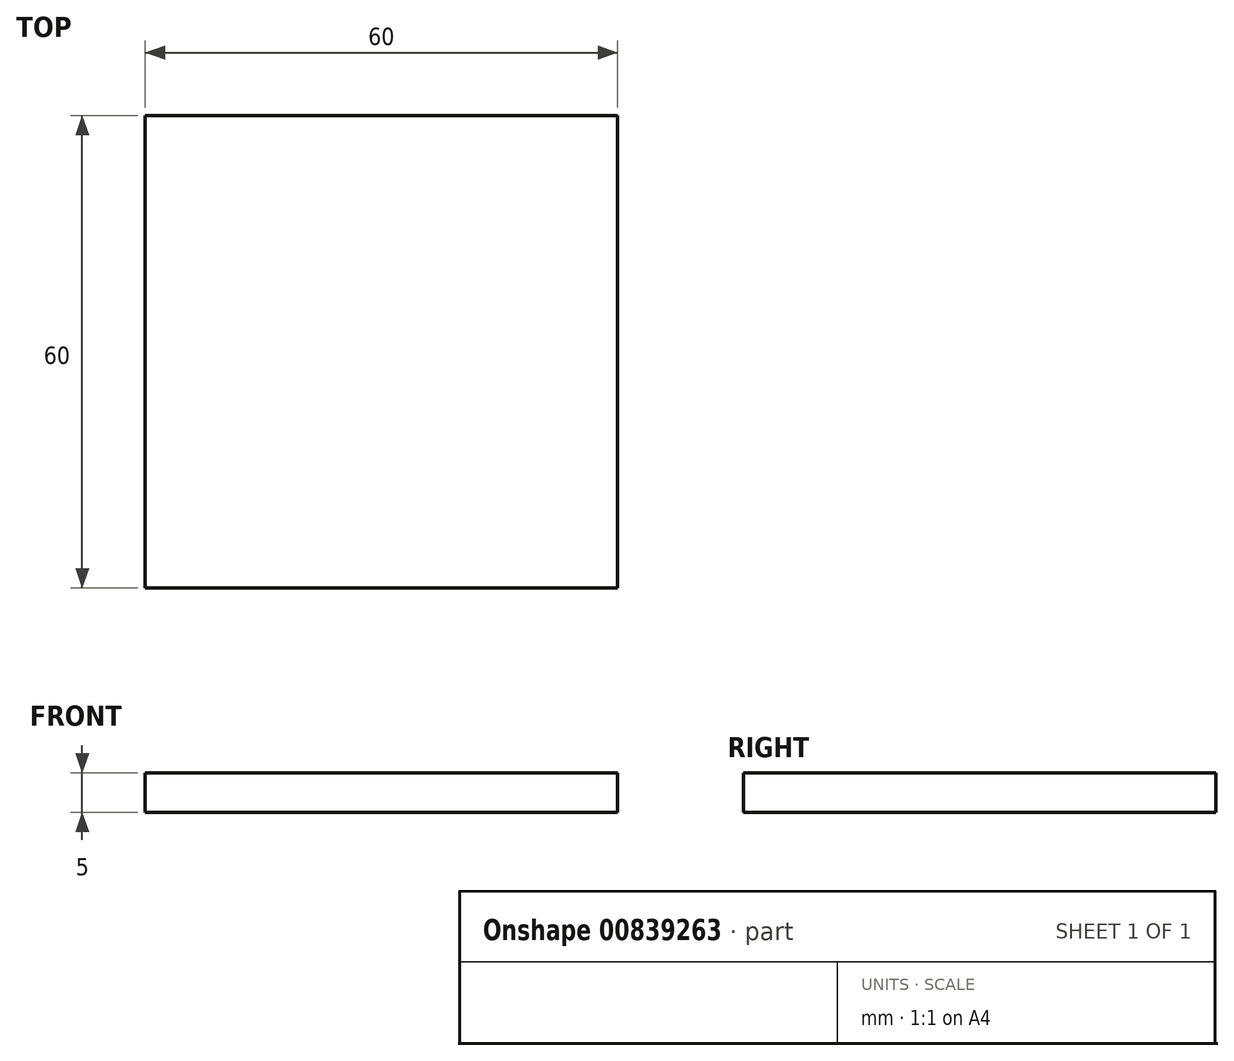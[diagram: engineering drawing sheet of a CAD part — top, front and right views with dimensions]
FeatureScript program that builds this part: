
annotation { "Feature Type Name" : "Feature", "Feature Type Description" : "" }
export const myFeature = defineFeature(function(context is Context, id is Id, definition is map)
    precondition{}
    {
        {
            var Q0;
            Q0=qCreatedBy(makeId("Top.planeOp"),FACE);
            var sketch = newSketch(context, id + "F0", { "sketchPlane" : qUnion([Q0])});
            skLineSegment(sketch, "E0.bottom", {"start": v(-26.32, 38.94) * mm, "end": v(33.68, 38.94) * mm});
            skLineSegment(sketch, "E0.top", {"start": v(-26.32, -21.06) * mm, "end": v(33.68, -21.06) * mm});
            skLineSegment(sketch, "E0.left", {"start": v(-26.32, 38.94) * mm, "end": v(-26.32, -21.06) * mm});
            skLineSegment(sketch, "E0.right", {"start": v(33.68, 38.94) * mm, "end": v(33.68, -21.06) * mm});
            skSolve(sketch);
        }
        {
            var Q0;
            Q0=makeQuery(id+"F0.imprint","IMPRINT",FACE,{"disambiguationData":[TD([[makeQuery(id+"F0.imprint","IMPRINT",EDGE,{"derivedFrom":sQuery(id+"F0.wireOp",EDGE,"E0.bottom")}),-1.0]])]});
            extrude(context, id + "F1", {"entities" : qUnion([Q0]), "depth" : 5 * mm, "offsetDistance" : 25 * mm});
        }
    });
